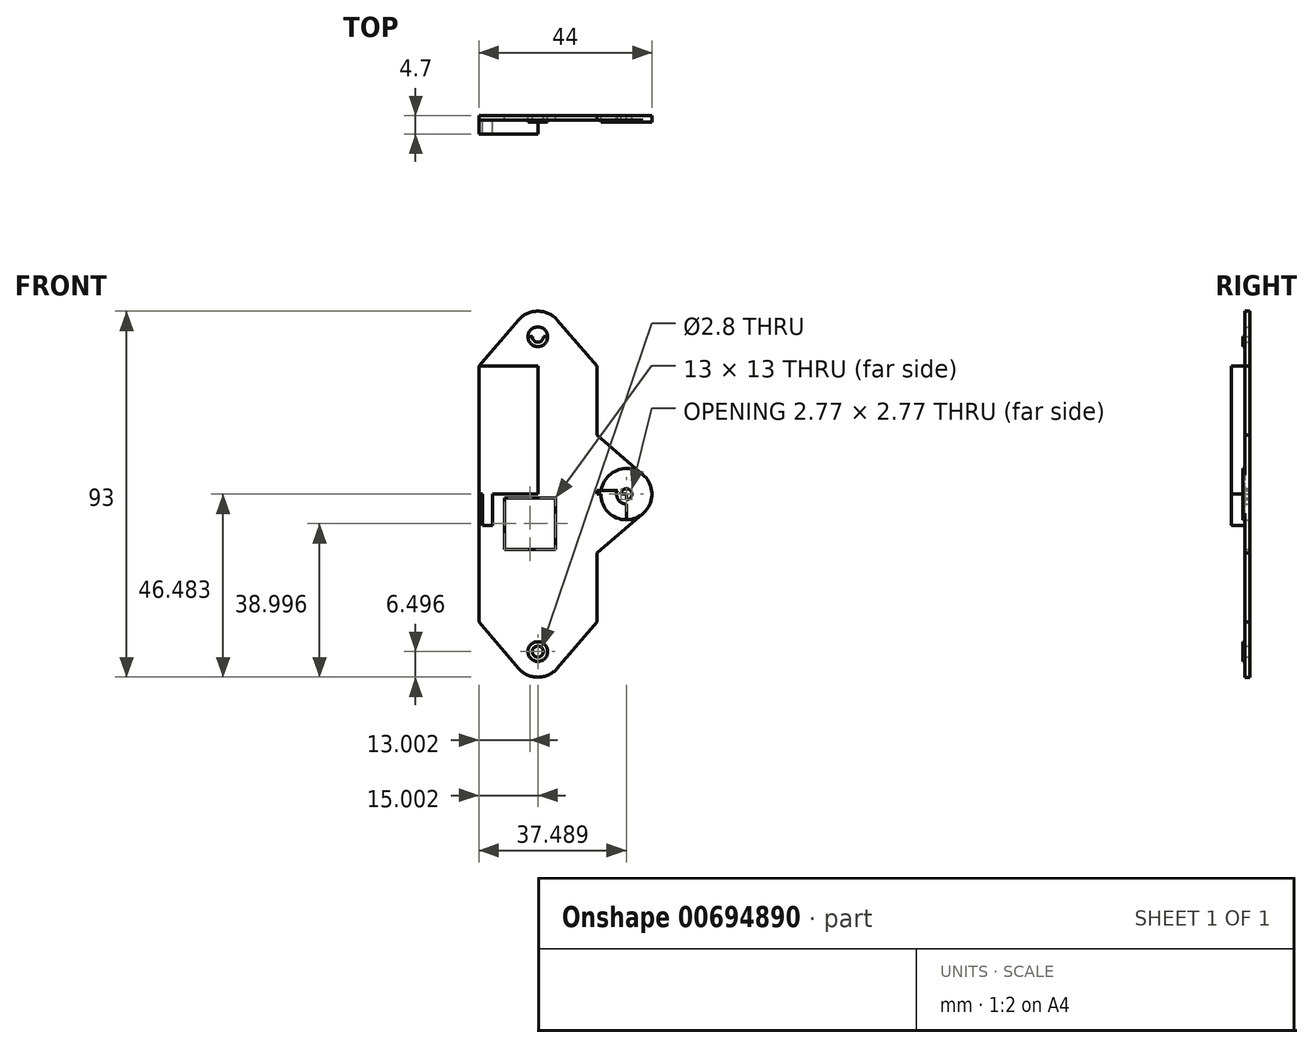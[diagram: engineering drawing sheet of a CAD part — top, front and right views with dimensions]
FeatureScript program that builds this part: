
annotation { "Feature Type Name" : "Feature", "Feature Type Description" : "" }
export const myFeature = defineFeature(function(context is Context, id is Id, definition is map)
    precondition{}
    {
        {
            var Q0;
            Q0=qCreatedBy(makeId("Front.planeOp"),FACE);
            var sketch = newSketch(context, id + "F0", { "sketchPlane" : qUnion([Q0])});
            skLineSegment(sketch, "E0", {"start": v(-6.36, 30.69) * mm, "end": v(-6.36, 38.19) * mm});
            skCircle(sketch, "E1", {"center": v(-6.36, 38.19) * mm, "radius": 6.5 * mm});
            skCircle(sketch, "E2", {"center": v(-6.36, 38.19) * mm, "radius": 2.5 * mm});
            skCircle(sketch, "E3", {"center": v(-6.36, 38.19) * mm, "radius": 1.4 * mm});
            skLineSegment(sketch, "E4", {"start": v(-6.36, 38.19) * mm, "end": v(-12.86, 38.19) * mm});
            skLineSegment(sketch, "E5", {"start": v(-12.86, 38.19) * mm, "end": v(0.14, 38.19) * mm});
            skLineSegment(sketch, "E6", {"start": v(0.14, 38.19) * mm, "end": v(0.14, 30.69) * mm});
            skLineSegment(sketch, "E7", {"start": v(-12.86, 30.69) * mm, "end": v(-12.86, 38.19) * mm});
            skLineSegment(sketch, "E8", {"start": v(-12.86, 30.69) * mm, "end": v(0.14, 30.69) * mm});
            skLineSegment(sketch, "E9", {"start": v(-12.86, 30.69) * mm, "end": v(-21.36, 30.69) * mm});
            skLineSegment(sketch, "E10", {"start": v(-21.36, 30.69) * mm, "end": v(-21.36, -34.31) * mm});
            skLineSegment(sketch, "E11", {"start": v(-6.36, 30.69) * mm, "end": v(-6.36, -34.31) * mm});
            skLineSegment(sketch, "E12", {"start": v(-6.36, -34.31) * mm, "end": v(-6.36, -41.81) * mm});
            skCircle(sketch, "E13", {"center": v(-6.36, -41.81) * mm, "radius": 6.5 * mm});
            skCircle(sketch, "E14", {"center": v(-6.36, -41.81) * mm, "radius": 2.5 * mm});
            skCircle(sketch, "E15", {"center": v(-6.36, -41.81) * mm, "radius": 1.4 * mm});
            skLineSegment(sketch, "E16", {"start": v(-6.36, -41.81) * mm, "end": v(-12.86, -41.81) * mm});
            skLineSegment(sketch, "E17", {"start": v(-12.86, -41.81) * mm, "end": v(0.14, -41.81) * mm});
            skLineSegment(sketch, "E18", {"start": v(0.14, -41.81) * mm, "end": v(0.14, -34.31) * mm});
            skLineSegment(sketch, "E19", {"start": v(-12.86, -41.81) * mm, "end": v(-12.86, -34.31) * mm});
            skLineSegment(sketch, "E20", {"start": v(0.14, -34.31) * mm, "end": v(8.64, -34.31) * mm});
            skLineSegment(sketch, "E21", {"start": v(8.64, -34.31) * mm, "end": v(-21.36, -34.31) * mm});
            skLineSegment(sketch, "E22", {"start": v(0.14, 30.69) * mm, "end": v(8.64, 30.69) * mm});
            skLineSegment(sketch, "E23", {"start": v(8.64, 30.69) * mm, "end": v(8.64, -34.31) * mm});
            skLineSegment(sketch, "E24", {"start": v(8.64, 30.69) * mm, "end": v(8.64, 4.69) * mm});
            skLineSegment(sketch, "E25", {"start": v(8.64, 4.69) * mm, "end": v(16.14, 4.69) * mm});
            skLineSegment(sketch, "E26", {"start": v(8.64, 4.69) * mm, "end": v(8.64, -8.31) * mm});
            skLineSegment(sketch, "E27", {"start": v(8.64, -8.31) * mm, "end": v(16.14, -8.31) * mm});
            skLineSegment(sketch, "E28", {"start": v(16.14, -8.31) * mm, "end": v(16.14, 4.69) * mm});
            skCircle(sketch, "E29", {"center": v(16.14, -1.81) * mm, "radius": 6.5 * mm});
            skCircle(sketch, "E30", {"center": v(16.14, -1.81) * mm, "radius": 2.5 * mm});
            skCircle(sketch, "E31", {"center": v(16.14, -1.81) * mm, "radius": 1.4 * mm});
            skLineSegment(sketch, "E32", {"start": v(-21.36, 30.69) * mm, "end": v(-11.3, 42.42) * mm});
            skLineSegment(sketch, "E33", {"start": v(-21.36, -34.31) * mm, "end": v(-11.1, -46.26) * mm});
            skLineSegment(sketch, "E34", {"start": v(8.64, -8.31) * mm, "end": v(8.64, -16.81) * mm});
            skLineSegment(sketch, "E35", {"start": v(8.64, 4.69) * mm, "end": v(8.64, 13.19) * mm});
            skLineSegment(sketch, "E36", {"start": v(8.64, -16.81) * mm, "end": v(20.37, -6.75) * mm});
            skLineSegment(sketch, "E37", {"start": v(8.64, 13.19) * mm, "end": v(20.37, 3.12) * mm});
            skLineSegment(sketch, "E38", {"start": v(8.64, -34.31) * mm, "end": v(-1.42, -46.05) * mm});
            skLineSegment(sketch, "E39", {"start": v(8.64, 30.69) * mm, "end": v(-1.42, 42.42) * mm});
            skLineSegment(sketch, "E40", {"start": v(-21.36, -1.81) * mm, "end": v(-17.86, -1.81) * mm});
            skLineSegment(sketch, "E41", {"start": v(-21.36, -1.81) * mm, "end": v(-20.36, -1.81) * mm});
            skLineSegment(sketch, "E42", {"start": v(1.57, -0.81) * mm, "end": v(7.03, -0.81) * mm});
            skLineSegment(sketch, "E43", {"start": v(7.03, -0.81) * mm, "end": v(16.14, -0.81) * mm});
            skLineSegment(sketch, "E44", {"start": v(16.14, -0.81) * mm, "end": v(-1.86, -0.81) * mm});
            skLineSegment(sketch, "E45", {"start": v(8.64, -34.31) * mm, "end": v(8.64, -16.81) * mm});
            skLineSegment(sketch, "E46", {"start": v(8.64, 13.19) * mm, "end": v(8.64, 30.69) * mm});
            skLineSegment(sketch, "E47", {"start": v(16.14, -1.81) * mm, "end": v(-21.36, -1.81) * mm});
            skLineSegment(sketch, "E48.MirrorCS", {"start": v(-14.86, -2.81) * mm, "end": v(-14.86, -15.81) * mm});
            skLineSegment(sketch, "E49.MirrorCS", {"start": v(-1.86, -2.81) * mm, "end": v(-14.86, -2.81) * mm});
            skLineSegment(sketch, "E50.MirrorCS", {"start": v(-1.86, -15.81) * mm, "end": v(-1.86, -2.81) * mm});
            skLineSegment(sketch, "E51.MirrorCS", {"start": v(-14.86, -15.81) * mm, "end": v(-1.86, -15.81) * mm});
            skLineSegment(sketch, "E52.MirrorCS", {"start": v(-20.36, -9.81) * mm, "end": v(-20.36, -1.81) * mm});
            skLineSegment(sketch, "E53.MirrorCS", {"start": v(-17.86, -1.81) * mm, "end": v(-17.86, -9.81) * mm});
            skLineSegment(sketch, "E54.MirrorCS", {"start": v(-17.86, -9.81) * mm, "end": v(-20.36, -9.81) * mm});
            skSolve(sketch);
        }
        {
            var Q0;
            Q0 = qSketchRegion(id + "F0", true);
            var Q1;
            {var subQ0=sQuery(id+"F0.wireOp",EDGE,"E1");var subQ1=sQuery(id+"F0.wireOp",EDGE,"E0");var subQ2=makeQuery(id+"F0.imprint","INTERSECT",VERTEX,{"derivedFrom":[subQ1,subQ0]});Q1=makeQuery(id+"F0.imprint","IMPRINT",FACE,{"disambiguationData":[TD([[makeQuery(id+"F0.imprint","IMPRINT",EDGE,{"disambiguationData":[TD([[subQ2,-1.0]])],"derivedFrom":subQ1}),1.0]])]});}
            var Q2;
            {var subQ5=sQuery(id+"F0.wireOp",EDGE,"E7");Q2=makeQuery(id+"F0.imprint","IMPRINT",FACE,{"disambiguationData":[TD([[makeQuery(id+"F0.imprint","IMPRINT",EDGE,{"derivedFrom":subQ5}),-1.0]])]});}
            var Q3;
            {var subQ1=sQuery(id+"F0.wireOp",EDGE,"E28");var subQ3=sQuery(id+"F0.wireOp",EDGE,"E30");var subQ4=makeQuery(id+"F0.imprint","INTERSECT",VERTEX,{"disambiguationData":[OD(0.0)],"derivedFrom":[subQ1,subQ3]});Q3=makeQuery(id+"F0.imprint","IMPRINT",FACE,{"disambiguationData":[TD([[makeQuery(id+"F0.imprint","IMPRINT",EDGE,{"disambiguationData":[TD([[subQ4,1.0]])],"derivedFrom":subQ3}),-1.0]])]});}
            var Q4;
            {var subQ0=sQuery(id+"F0.wireOp",EDGE,"E25");Q4=makeQuery(id+"F0.imprint","IMPRINT",FACE,{"disambiguationData":[TD([[makeQuery(id+"F0.imprint","IMPRINT",EDGE,{"derivedFrom":subQ0}),-1.0]])]});}
            var Q5;
            {var subQ5=sQuery(id+"F0.wireOp",EDGE,"E18");Q5=makeQuery(id+"F0.imprint","IMPRINT",FACE,{"disambiguationData":[TD([[makeQuery(id+"F0.imprint","IMPRINT",EDGE,{"derivedFrom":subQ5}),1.0]])]});}
            var Q6;
            {var subQ5=sQuery(id+"F0.wireOp",EDGE,"E19");Q6=makeQuery(id+"F0.imprint","IMPRINT",FACE,{"disambiguationData":[TD([[makeQuery(id+"F0.imprint","IMPRINT",EDGE,{"derivedFrom":subQ5}),-1.0]])]});}
            var Q7;
            {var subQ0=sQuery(id+"F0.wireOp",EDGE,"E13");var subQ1=sQuery(id+"F0.wireOp",EDGE,"E12");var subQ2=makeQuery(id+"F0.imprint","INTERSECT",VERTEX,{"derivedFrom":[subQ1,subQ0]});Q7=makeQuery(id+"F0.imprint","IMPRINT",FACE,{"disambiguationData":[TD([[makeQuery(id+"F0.imprint","IMPRINT",EDGE,{"disambiguationData":[TD([[subQ2,-1.0]])],"derivedFrom":subQ1}),-1.0]])]});}
            var Q8;
            {var subQ0=sQuery(id+"F0.wireOp",EDGE,"E13");var subQ1=sQuery(id+"F0.wireOp",EDGE,"E12");var subQ2=makeQuery(id+"F0.imprint","INTERSECT",VERTEX,{"derivedFrom":[subQ1,subQ0]});Q8=makeQuery(id+"F0.imprint","IMPRINT",FACE,{"disambiguationData":[TD([[makeQuery(id+"F0.imprint","IMPRINT",EDGE,{"disambiguationData":[TD([[subQ2,-1.0]])],"derivedFrom":subQ1}),1.0]])]});}
            var Q9;
            {var subQ5=sQuery(id+"F0.wireOp",EDGE,"E6");Q9=makeQuery(id+"F0.imprint","IMPRINT",FACE,{"disambiguationData":[TD([[makeQuery(id+"F0.imprint","IMPRINT",EDGE,{"derivedFrom":subQ5}),-1.0]])]});}
            var Q10;
            {var subQ0=sQuery(id+"F0.wireOp",EDGE,"E1");var subQ1=sQuery(id+"F0.wireOp",EDGE,"E0");var subQ2=makeQuery(id+"F0.imprint","INTERSECT",VERTEX,{"derivedFrom":[subQ1,subQ0]});Q10=makeQuery(id+"F0.imprint","IMPRINT",FACE,{"disambiguationData":[TD([[makeQuery(id+"F0.imprint","IMPRINT",EDGE,{"disambiguationData":[TD([[subQ2,-1.0]])],"derivedFrom":subQ1}),-1.0]])]});}
            var Q11;
            {var subQ0=sQuery(id+"F0.wireOp",EDGE,"E27");Q11=makeQuery(id+"F0.imprint","IMPRINT",FACE,{"disambiguationData":[TD([[makeQuery(id+"F0.imprint","IMPRINT",EDGE,{"derivedFrom":subQ0}),1.0]])]});}
            var Q12;
            {var subQ1=sQuery(id+"F0.wireOp",EDGE,"E28");var subQ3=sQuery(id+"F0.wireOp",EDGE,"E30");var subQ4=makeQuery(id+"F0.imprint","INTERSECT",VERTEX,{"disambiguationData":[OD(1.0)],"derivedFrom":[subQ1,subQ3]});Q12=makeQuery(id+"F0.imprint","IMPRINT",FACE,{"disambiguationData":[TD([[makeQuery(id+"F0.imprint","IMPRINT",EDGE,{"disambiguationData":[TD([[subQ4,-1.0]])],"derivedFrom":subQ3}),-1.0]])]});}
            var Q13;
            {var subQ0=sQuery(id+"F0.wireOp",EDGE,"E44");var subQ1=sQuery(id+"F0.wireOp",EDGE,"E29");var subQ2=makeQuery(id+"F0.imprint","INTERSECT",VERTEX,{"derivedFrom":[subQ1,subQ0]});Q13=makeQuery(id+"F0.imprint","IMPRINT",FACE,{"disambiguationData":[TD([[makeQuery(id+"F0.imprint","IMPRINT",EDGE,{"disambiguationData":[TD([[subQ2,-1.0]])],"derivedFrom":subQ1}),1.0]])]});}
            var Q14;
            {var subQ0=sQuery(id+"F0.wireOp",EDGE,"E44");var subQ1=sQuery(id+"F0.wireOp",EDGE,"E26");var subQ2=makeQuery(id+"F0.imprint","INTERSECT",VERTEX,{"derivedFrom":[subQ1,subQ0]});Q14=makeQuery(id+"F0.imprint","IMPRINT",FACE,{"disambiguationData":[TD([[makeQuery(id+"F0.imprint","IMPRINT",EDGE,{"disambiguationData":[TD([[subQ2,-1.0]])],"derivedFrom":subQ1}),1.0]])]});}
            extrude(context, id + "F1", {"entities" : qUnion([Q0, Q1, Q2, Q3, Q4, Q5, Q6, Q7, Q8, Q9, Q10, Q11, Q12, Q13, Q14]), "depth" : 1.2 * mm, "offsetDistance" : 25 * mm});
        }
        {
            var Q0;
            {var subQ0=sQuery(id+"F0.wireOp",EDGE,"E2");var subQ1=sQuery(id+"F0.wireOp",EDGE,"E0");var subQ2=makeQuery(id+"F0.imprint","INTERSECT",VERTEX,{"derivedFrom":[subQ1,subQ0]});Q0=makeQuery(id+"F0.imprint","IMPRINT",FACE,{"disambiguationData":[TD([[makeQuery(id+"F0.imprint","IMPRINT",EDGE,{"disambiguationData":[TD([[subQ2,-1.0]])],"derivedFrom":subQ1}),-1.0]])]});}
            var Q1;
            {var subQ0=sQuery(id+"F0.wireOp",EDGE,"E5");var subQ1=sQuery(id+"F0.wireOp",EDGE,"E2");var subQ2=makeQuery(id+"F0.imprint","INTERSECT",VERTEX,{"disambiguationData":[OD(0.0)],"derivedFrom":[subQ1,subQ0]});Q1=makeQuery(id+"F0.imprint","IMPRINT",FACE,{"disambiguationData":[TD([[makeQuery(id+"F0.imprint","IMPRINT",EDGE,{"disambiguationData":[TD([[subQ2,1.0]])],"derivedFrom":subQ1}),1.0]])]});}
            var Q2;
            {var subQ0=sQuery(id+"F0.wireOp",EDGE,"E2");var subQ1=sQuery(id+"F0.wireOp",EDGE,"E0");var subQ2=makeQuery(id+"F0.imprint","INTERSECT",VERTEX,{"derivedFrom":[subQ1,subQ0]});Q2=makeQuery(id+"F0.imprint","IMPRINT",FACE,{"disambiguationData":[TD([[makeQuery(id+"F0.imprint","IMPRINT",EDGE,{"disambiguationData":[TD([[subQ2,-1.0]])],"derivedFrom":subQ1}),1.0]])]});}
            var Q3;
            {var subQ0=sQuery(id+"F0.wireOp",EDGE,"E30");var subQ1=sQuery(id+"F0.wireOp",EDGE,"E28");var subQ2=makeQuery(id+"F0.imprint","INTERSECT",VERTEX,{"disambiguationData":[OD(0.0)],"derivedFrom":[subQ1,subQ0]});Q3=makeQuery(id+"F0.imprint","IMPRINT",FACE,{"disambiguationData":[TD([[makeQuery(id+"F0.imprint","IMPRINT",EDGE,{"disambiguationData":[TD([[subQ2,-1.0]])],"derivedFrom":subQ1}),1.0]])]});}
            var Q4;
            {var subQ0=sQuery(id+"F0.wireOp",EDGE,"E30");var subQ1=sQuery(id+"F0.wireOp",EDGE,"E28");var subQ2=makeQuery(id+"F0.imprint","INTERSECT",VERTEX,{"disambiguationData":[OD(0.0)],"derivedFrom":[subQ1,subQ0]});Q4=makeQuery(id+"F0.imprint","IMPRINT",FACE,{"disambiguationData":[TD([[makeQuery(id+"F0.imprint","IMPRINT",EDGE,{"disambiguationData":[TD([[subQ2,-1.0]])],"derivedFrom":subQ1}),-1.0]])]});}
            var Q5;
            {var subQ0=sQuery(id+"F0.wireOp",EDGE,"E17");var subQ1=sQuery(id+"F0.wireOp",EDGE,"E14");var subQ2=makeQuery(id+"F0.imprint","INTERSECT",VERTEX,{"disambiguationData":[OD(0.0)],"derivedFrom":[subQ1,subQ0]});Q5=makeQuery(id+"F0.imprint","IMPRINT",FACE,{"disambiguationData":[TD([[makeQuery(id+"F0.imprint","IMPRINT",EDGE,{"disambiguationData":[TD([[subQ2,1.0]])],"derivedFrom":subQ1}),1.0]])]});}
            var Q6;
            {var subQ0=sQuery(id+"F0.wireOp",EDGE,"E14");var subQ1=sQuery(id+"F0.wireOp",EDGE,"E12");var subQ2=makeQuery(id+"F0.imprint","INTERSECT",VERTEX,{"derivedFrom":[subQ1,subQ0]});Q6=makeQuery(id+"F0.imprint","IMPRINT",FACE,{"disambiguationData":[TD([[makeQuery(id+"F0.imprint","IMPRINT",EDGE,{"disambiguationData":[TD([[subQ2,-1.0]])],"derivedFrom":subQ1}),-1.0]])]});}
            var Q7;
            {var subQ0=sQuery(id+"F0.wireOp",EDGE,"E14");var subQ1=sQuery(id+"F0.wireOp",EDGE,"E12");var subQ2=makeQuery(id+"F0.imprint","INTERSECT",VERTEX,{"derivedFrom":[subQ1,subQ0]});Q7=makeQuery(id+"F0.imprint","IMPRINT",FACE,{"disambiguationData":[TD([[makeQuery(id+"F0.imprint","IMPRINT",EDGE,{"disambiguationData":[TD([[subQ2,-1.0]])],"derivedFrom":subQ1}),1.0]])]});}
            var Q8;
            {var subQ0=sQuery(id+"F0.wireOp",EDGE,"E31");var subQ1=sQuery(id+"F0.wireOp",EDGE,"E28");var subQ2=makeQuery(id+"F0.imprint","INTERSECT",VERTEX,{"disambiguationData":[OD(1.0)],"derivedFrom":[subQ1,subQ0]});Q8=makeQuery(id+"F0.imprint","IMPRINT",FACE,{"disambiguationData":[TD([[makeQuery(id+"F0.imprint","IMPRINT",EDGE,{"disambiguationData":[TD([[subQ2,-1.0]])],"derivedFrom":subQ1}),1.0]])]});}
            var Q9;
            {var subQ0=sQuery(id+"F0.wireOp",EDGE,"E44");var subQ1=sQuery(id+"F0.wireOp",EDGE,"E30");var subQ2=makeQuery(id+"F0.imprint","INTERSECT",VERTEX,{"derivedFrom":[subQ1,subQ0]});Q9=makeQuery(id+"F0.imprint","IMPRINT",FACE,{"disambiguationData":[TD([[makeQuery(id+"F0.imprint","IMPRINT",EDGE,{"disambiguationData":[TD([[subQ2,-1.0]])],"derivedFrom":subQ1}),1.0]])]});}
            extrude(context, id + "F2", {"entities" : qUnion([Q0, Q1, Q2, Q3, Q4, Q5, Q6, Q7, Q8, Q9]), "operationType" : NewBodyOperationType.ADD, "depth" : 1.7 * mm, "offsetDistance" : 25 * mm});
        }
        {
            var Q0;
            Q0=makeQuery(id+"F0.imprint","IMPRINT",FACE,{"disambiguationData":[TD([[makeQuery(id+"F0.imprint","IMPRINT",EDGE,{"derivedFrom":sQuery(id+"F0.wireOp",EDGE,"E40")}),1.0]])]});
            var Q1;
            {var subQ0=sQuery(id+"F0.wireOp",EDGE,"E52.MirrorCS");Q1=makeQuery(id+"F0.imprint","IMPRINT",FACE,{"disambiguationData":[TD([[makeQuery(id+"F0.imprint","IMPRINT",EDGE,{"derivedFrom":subQ0}),-1.0]])]});}
            extrude(context, id + "F3", {"entities" : qUnion([Q0, Q1]), "operationType" : NewBodyOperationType.ADD, "depth" : 4.7 * mm, "offsetDistance" : 25 * mm});
        }
    });
